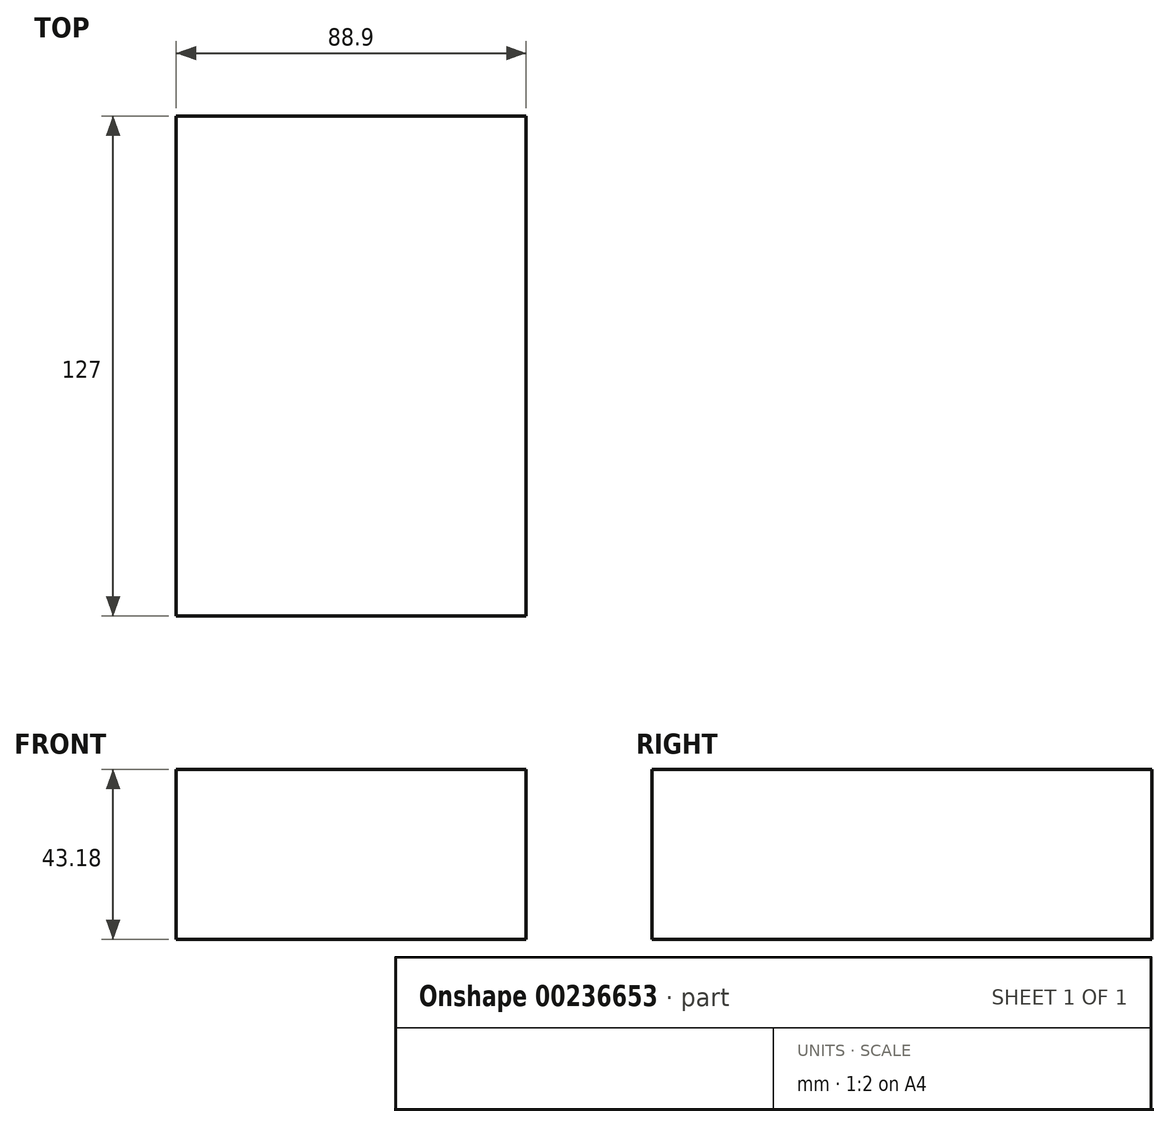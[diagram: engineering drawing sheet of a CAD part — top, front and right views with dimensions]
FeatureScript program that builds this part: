
annotation { "Feature Type Name" : "Feature", "Feature Type Description" : "" }
export const myFeature = defineFeature(function(context is Context, id is Id, definition is map)
    precondition{}
    {
        {
            var Q0;
            Q0=qCreatedBy(makeId("Front.planeOp"),FACE);
            var sketch = newSketch(context, id + "F0", { "sketchPlane" : qUnion([Q0])});
            skLineSegment(sketch, "E0.bottom", {"start": v(44.45, 21.6) * mm, "end": v(-44.45, 21.59) * mm});
            skLineSegment(sketch, "E0.top", {"start": v(44.45, -21.59) * mm, "end": v(-44.45, -21.6) * mm});
            skLineSegment(sketch, "E0.left", {"start": v(44.45, 21.6) * mm, "end": v(44.45, -21.59) * mm});
            skLineSegment(sketch, "E0.right", {"start": v(-44.45, 21.59) * mm, "end": v(-44.45, -21.6) * mm});
            skPoint(sketch, "E0.middle", {"position": v(0, 0) * mm});
            skLineSegment(sketch, "E1.bottom", {"start": v(121.57, 85.1) * mm, "end": v(91.09, 85.1) * mm});
            skLineSegment(sketch, "E1.top", {"start": v(121.57, 105.41) * mm, "end": v(91.09, 105.41) * mm});
            skLineSegment(sketch, "E1.left", {"start": v(121.57, 85.1) * mm, "end": v(121.57, 105.41) * mm});
            skLineSegment(sketch, "E1.right", {"start": v(91.09, 85.1) * mm, "end": v(91.09, 105.41) * mm});
            skPoint(sketch, "E1.middle", {"position": v(106.33, 95.25) * mm});
            skLineSegment(sketch, "E2", {"start": v(44.45, 21.6) * mm, "end": v(44.45, 69.85) * mm});
            skArc(sketch, "E3", {"start": v(44.45, 69.85) * mm, "mid": v(50.21, 83.76) * mm, "end": v(64.12, 89.52) * mm});
            skLineSegment(sketch, "E4", {"start": v(64.12, 89.52) * mm, "end": v(104.76, 89.52) * mm});
            skLineSegment(sketch, "E5.0", {"start": v(64.12, 98.54) * mm, "end": v(104.76, 98.54) * mm});
            skArc(sketch, "E5.1", {"start": v(35.43, 69.85) * mm, "mid": v(43.84, 90.14) * mm, "end": v(64.12, 98.54) * mm});
            skLineSegment(sketch, "E5.2", {"start": v(35.43, 21.6) * mm, "end": v(35.43, 69.85) * mm});
            skFitSpline(sketch, "E6", {"points": [v(-44.45, 21.59) * mm, v(91.09, 105.41) * mm], "startDerivative": vector(145.82, 37.62) * mm, "endDerivative": vector(171.65, -91.12) * mm});
            skSolve(sketch);
        }
        {
            var Q0;
            Q0=makeQuery(id+"F0.imprint","IMPRINT",FACE,{"disambiguationData":[TD([[makeQuery(id+"F0.imprint","IMPRINT",EDGE,{"derivedFrom":sQuery(id+"F0.wireOp",EDGE,"E0.top")}),-1.0]])]});
            extrude(context, id + "F1", {"entities" : qUnion([Q0]), "endBound" : BoundingType.SYMMETRIC, "depth" : 127 * mm});
        }
    });
